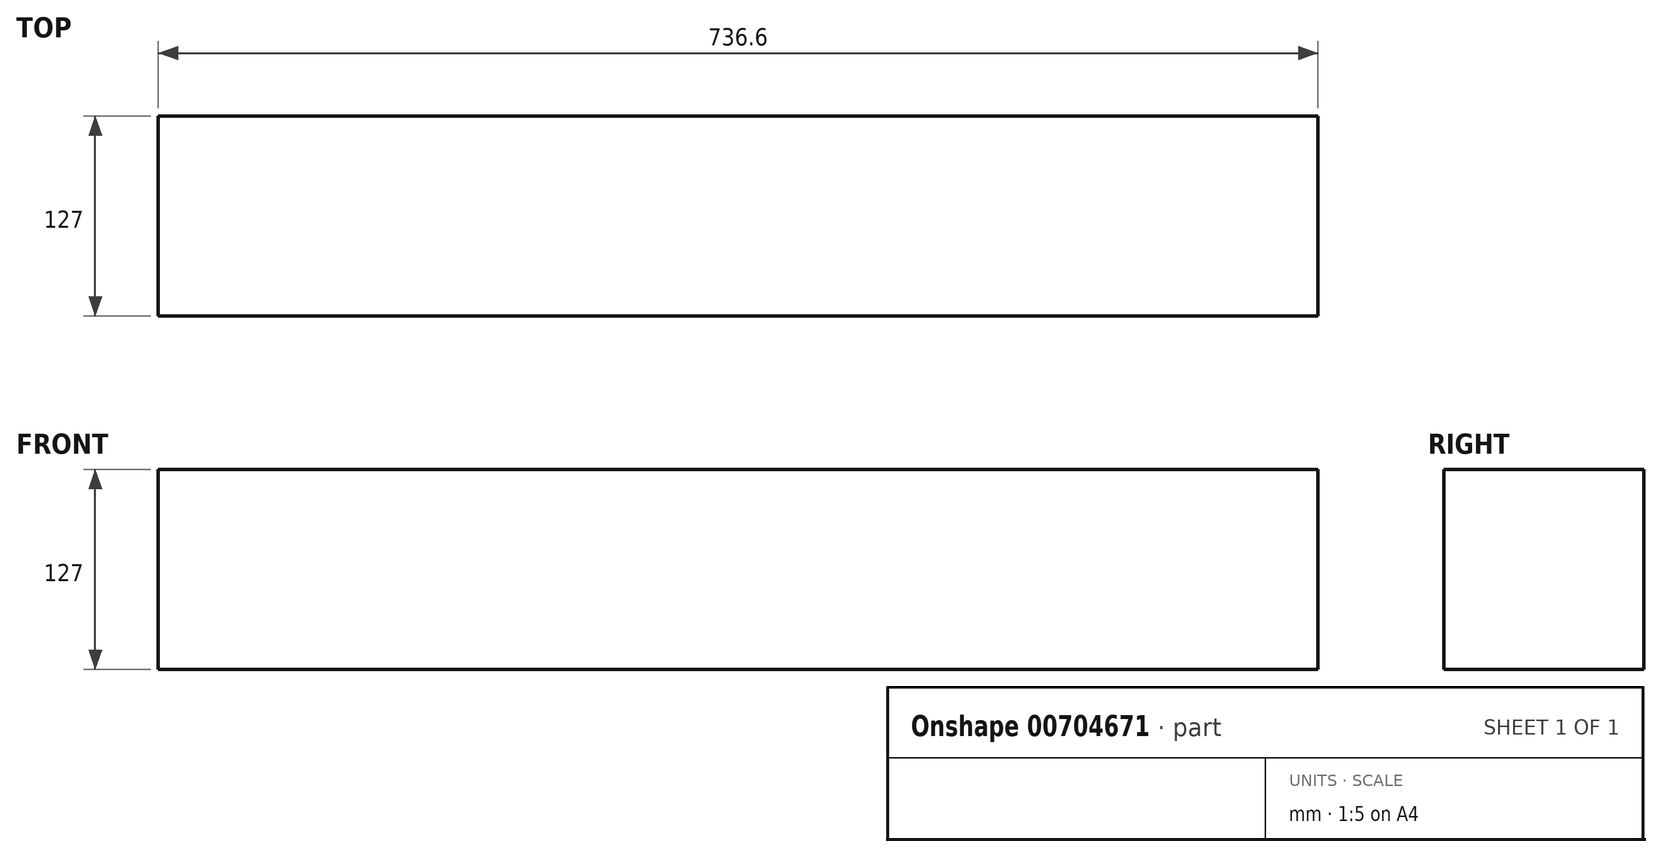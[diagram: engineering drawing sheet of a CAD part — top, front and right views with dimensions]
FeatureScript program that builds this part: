
annotation { "Feature Type Name" : "Feature", "Feature Type Description" : "" }
export const myFeature = defineFeature(function(context is Context, id is Id, definition is map)
    precondition{}
    {
        {
            var Q0;
            Q0=qCreatedBy(makeId("Top.planeOp"),FACE);
            var sketch = newSketch(context, id + "F0", { "sketchPlane" : qUnion([Q0])});
            skLineSegment(sketch, "E0.bottom", {"start": v(173.07, 127) * mm, "end": v(-563.53, 127) * mm});
            skLineSegment(sketch, "E0.top", {"start": v(173.07, 0) * mm, "end": v(-563.53, 0) * mm});
            skLineSegment(sketch, "E0.left", {"start": v(173.07, 127) * mm, "end": v(173.07, 0) * mm});
            skLineSegment(sketch, "E0.right", {"start": v(-563.53, 127) * mm, "end": v(-563.53, 0) * mm});
            skSolve(sketch);
        }
        {
            var Q0;
            Q0 = qSketchRegion(id + "F0", true);
            extrude(context, id + "F1", {"entities" : qUnion([Q0]), "depth" : 127 * mm, "offsetDistance" : 25.4 * mm});
        }
    });
